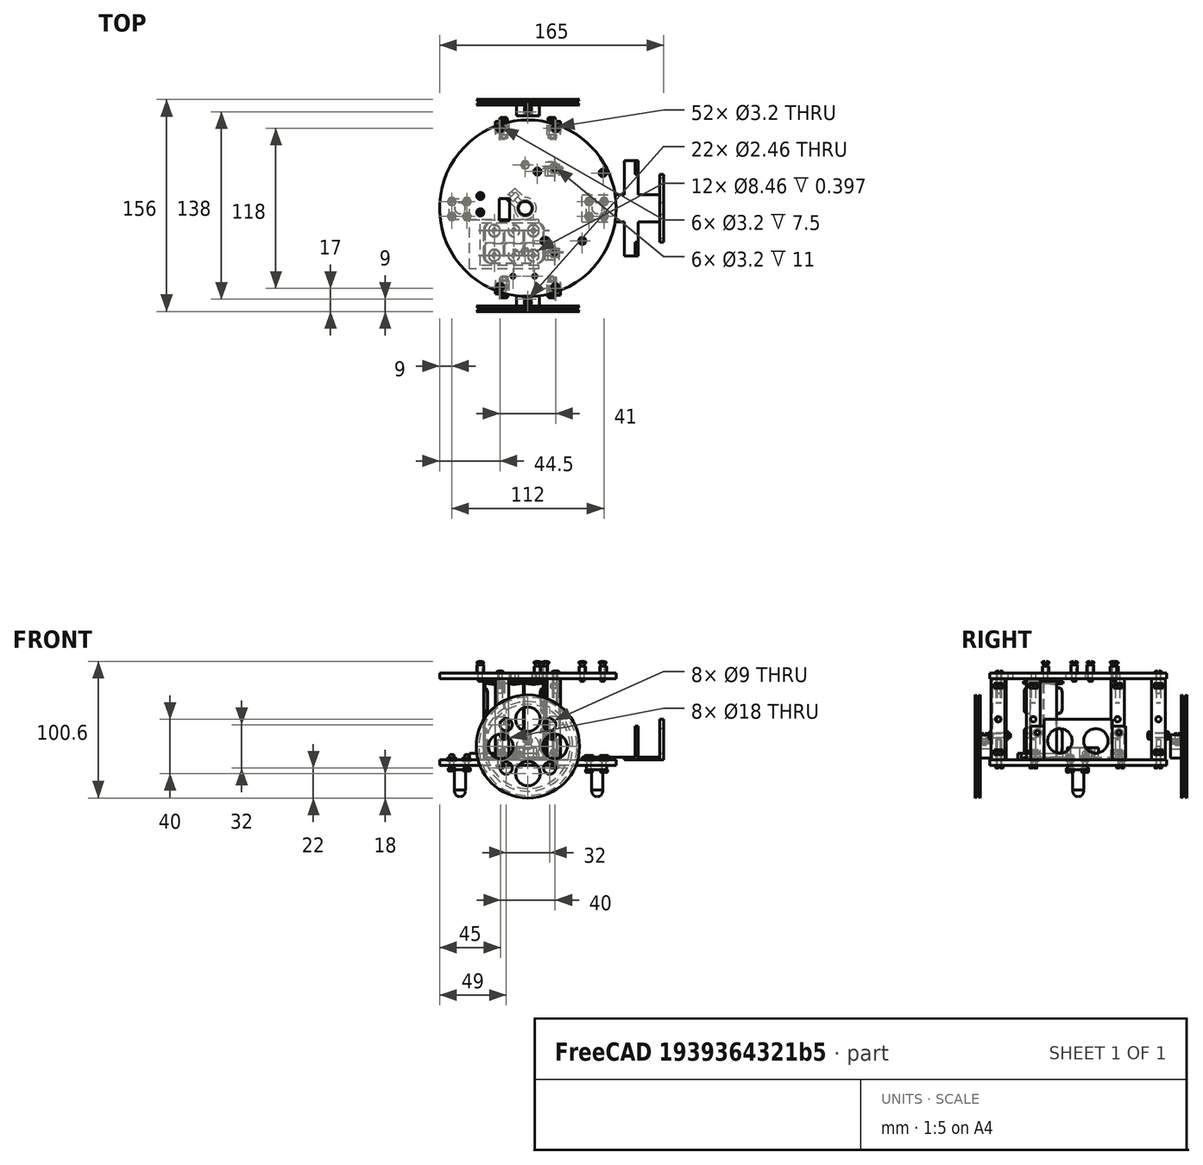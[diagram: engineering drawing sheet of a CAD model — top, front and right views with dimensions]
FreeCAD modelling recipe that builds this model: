
FCSTD DOCUMENT  (FreeCAD 0.21R33668 +26 (Git))
Label: ANIMARUEDASYARDUINO
License: All rights reserved
LicenseURL: https://en.wikipedia.org/wiki/All_rights_reserved
objects: Part::FeaturePython×56, App::DocumentObjectGroupPython×29, Part::MultiFuse×17, Part::Feature×14, Mesh::Feature×5
note: 87 computed .brp shape members not serialized (recipe doc carries the construction recipe); baked Part::Feature solids carry a one-line shape summary decoded from their .brp

FEATURE [Part::Feature] Cut009_solid  label="ballCSensor"
  Placement = pos=(0,0,20) rot=(0,0,1;0rad)
  shape: bbox 15 x 15 x 23 mm, 13 faces (baked)
FEATURE [Part::Feature] Fusion060_solid  label="plataformaInferior (Solid)"
  Placement = pos=(0,0,20) rot=(0,0,1;0rad)
  shape: bbox 130 x 130 x 13 mm, 195 faces (baked)
FEATURE [Part::FeaturePython] Nut  label="M3-Tuerca"  # Fasteners workbench fastener (typed FeaturePython)
  Placement = pos=(41,5,8) rot=(0,0,1;0rad)
  diameter = 4
  invert = false
  leftHanded = false
  matchOuter = false
  offset = 0
  thread = false
  type = 22
FEATURE [Part::FeaturePython] Nut001  label="M3-Tuerca004"  # Fasteners workbench fastener (typed FeaturePython)
  Placement = pos=(52,5,8) rot=(0,0,1;0rad)
  diameter = 4
  invert = false
  leftHanded = false
  matchOuter = false
  offset = 0
  thread = false
  type = 22
FEATURE [Part::FeaturePython] Nut002  label="M3-Tuerca006"  # Fasteners workbench fastener (typed FeaturePython)
  Placement = pos=(52,-6,8) rot=(0,0,1;0rad)
  diameter = 4
  invert = false
  leftHanded = false
  matchOuter = false
  offset = 0
  thread = false
  type = 22
FEATURE [Part::FeaturePython] Nut003  label="M3-Tuerca005"  # Fasteners workbench fastener (typed FeaturePython)
  Placement = pos=(41,-6,8) rot=(0,0,1;0rad)
  diameter = 4
  invert = false
  leftHanded = false
  matchOuter = false
  offset = 0
  thread = false
  type = 22
FEATURE [Part::MultiFuse] Fusion  label="tuercasBallCSensor"
  Placement = pos=(0,0,2) rot=(0,0,1;0rad)
  Shapes = -> [Nut,Nut001,Nut002,Nut003]
FEATURE [Part::FeaturePython] Nut004  label="M3-Tuerca007"  # Fasteners workbench fastener (typed FeaturePython)
  Placement = pos=(41,5,8) rot=(0,0,1;0rad)
  diameter = 4
  invert = false
  leftHanded = false
  matchOuter = false
  offset = 0
  thread = false
  type = 22
FEATURE [Part::FeaturePython] Nut005  label="M3-Tuerca008"  # Fasteners workbench fastener (typed FeaturePython)
  Placement = pos=(52,5,8) rot=(0,0,1;0rad)
  diameter = 4
  invert = false
  leftHanded = false
  matchOuter = false
  offset = 0
  thread = false
  type = 22
FEATURE [Part::FeaturePython] Nut006  label="M3-Tuerca009"  # Fasteners workbench fastener (typed FeaturePython)
  Placement = pos=(52,-6,8) rot=(0,0,1;0rad)
  diameter = 4
  invert = false
  leftHanded = false
  matchOuter = false
  offset = 0
  thread = false
  type = 22
FEATURE [Part::FeaturePython] Nut007  label="M3-Tuerca010"  # Fasteners workbench fastener (typed FeaturePython)
  Placement = pos=(41,-6,8) rot=(0,0,1;0rad)
  diameter = 4
  invert = false
  leftHanded = false
  matchOuter = false
  offset = 0
  thread = false
  type = 22
FEATURE [Part::MultiFuse] Fusion001  label="tuercasBallCLibre"
  Placement = pos=(-101,0,0) rot=(0,0,1;0rad)
  Shapes = -> [Nut004,Nut005,Nut006,Nut007]
FEATURE [Part::Feature] Cut009_solid001  label="ballCLibre"
  Placement = pos=(-101,0,20) rot=(0,0,1;0rad)
  shape: bbox 15 x 15 x 23 mm, 13 faces (baked)
FEATURE [Part::Feature] Cut_solid  label="soporteSensores (Solid)"
  Placement = pos=(15,0,20) rot=(0,0,1;0rad)
  shape: bbox 60 x 70 x 30 mm, 144 faces (baked)
FEATURE [Part::FeaturePython] Screw  label="M3x10-Tornillo"  # Fasteners workbench fastener (typed FeaturePython)
  Placement = pos=(-60,5,3) rot=(1,0,0;3.14159rad)
  diameter = 4
  invert = false
  leftHanded = false
  length = 4
  lengthCustom = 10
  matchOuter = false
  offset = 0
  thread = false
  type = 30
FEATURE [Part::FeaturePython] Screw001  label="M3x10-Tornillo001"  # Fasteners workbench fastener (typed FeaturePython)
  Placement = pos=(-60,-6,3) rot=(1,0,0;3.14159rad)
  diameter = 4
  invert = false
  leftHanded = false
  length = 4
  lengthCustom = 10
  matchOuter = false
  offset = 0
  thread = false
  type = 30
FEATURE [Part::FeaturePython] Screw002  label="M3x10-Tornillo002"  # Fasteners workbench fastener (typed FeaturePython)
  Placement = pos=(-49,-6,3) rot=(1,0,0;3.14159rad)
  diameter = 4
  invert = false
  leftHanded = false
  length = 4
  lengthCustom = 10
  matchOuter = false
  offset = 0
  thread = false
  type = 30
FEATURE [Part::FeaturePython] Screw003  label="M3x10-Tornillo003"  # Fasteners workbench fastener (typed FeaturePython)
  Placement = pos=(-49,5,3) rot=(1,0,0;3.14159rad)
  diameter = 4
  invert = false
  leftHanded = false
  length = 4
  lengthCustom = 10
  matchOuter = false
  offset = 0
  thread = false
  type = 30
FEATURE [Part::MultiFuse] Fusion002  label="tornillosBallClibre"
  Shapes = -> [Screw,Screw001,Screw002,Screw003]
FEATURE [Part::FeaturePython] Screw004  label="M3x10-Tornillo004"  # Fasteners workbench fastener (typed FeaturePython)
  Placement = pos=(-60,5,3) rot=(1,0,0;3.14159rad)
  diameter = 4
  invert = false
  leftHanded = false
  length = 4
  lengthCustom = 10
  matchOuter = false
  offset = 0
  thread = false
  type = 30
FEATURE [Part::FeaturePython] Screw005  label="M3x10-Tornillo005"  # Fasteners workbench fastener (typed FeaturePython)
  Placement = pos=(-60,-6,3) rot=(1,0,0;3.14159rad)
  diameter = 4
  invert = false
  leftHanded = false
  length = 4
  lengthCustom = 10
  matchOuter = false
  offset = 0
  thread = false
  type = 30
FEATURE [Part::FeaturePython] Screw006  label="M3x10-Tornillo006"  # Fasteners workbench fastener (typed FeaturePython)
  Placement = pos=(-49,-6,3) rot=(1,0,0;3.14159rad)
  diameter = 4
  invert = false
  leftHanded = false
  length = 4
  lengthCustom = 10
  matchOuter = false
  offset = 0
  thread = false
  type = 30
FEATURE [Part::FeaturePython] Screw007  label="M3x10-Tornillo007"  # Fasteners workbench fastener (typed FeaturePython)
  Placement = pos=(-49,5,3) rot=(1,0,0;3.14159rad)
  diameter = 4
  invert = false
  leftHanded = false
  length = 4
  lengthCustom = 10
  matchOuter = false
  offset = 0
  thread = false
  type = 30
FEATURE [Part::MultiFuse] Fusion003  label="tornillosBallCSensor"
  Placement = pos=(101,0,-1) rot=(0,0,1;0rad)
  Shapes = -> [Screw004,Screw005,Screw006,Screw007]
FEATURE [App::DocumentObjectGroupPython] SimpleGroup  # scripted group (container) (typed FeaturePython)
  AnimationStepTime = 0
  AnimationSteps = 20
  Distance = 19
  Revolutions = 0
  dir_vectors = (1) [(0,0,1)]
  rot_centers = (1) [(-54.5,-0.5,-14)]
  rot_vectors = (1) [(0,0,1)]
FEATURE [App::DocumentObjectGroupPython] SimpleGroup003  # scripted group (container) (typed FeaturePython)
  AnimationStepTime = 0
  AnimationSteps = 20
  Distance = 20
  Revolutions = 0
  dir_vectors = (1) [(0,0,-1)]
  rot_centers = (1) [(-60,-6,26)]
  rot_vectors = (1) [(0,0,-1)]
FEATURE [App::DocumentObjectGroupPython] SimpleGroup004  # scripted group (container) (typed FeaturePython)
  AnimationStepTime = 0
  AnimationSteps = 20
  Distance = 40
  Revolutions = 0
  dir_vectors = (1) [(0,1.22465e-16,1)]
  rot_centers = (1) [(-60,5,-27)]
  rot_vectors = (1) [(0,1.22465e-16,1)]
FEATURE [App::DocumentObjectGroupPython] SimpleGroup005  # scripted group (container) (typed FeaturePython)
  AnimationStepTime = 0
  AnimationSteps = 20
  Distance = 19
  Revolutions = 0
  dir_vectors = (1) [(0,0,1)]
  rot_centers = (1) [(46.5,-0.5,-14)]
  rot_vectors = (1) [(0,0,1)]
FEATURE [Part::Feature] Part__Feature  label="6 x AAA Holder"
  Placement = pos=(-100,212,67) rot=(0.57735,0.57735,-0.57735;2.0944rad)
  shape: bbox 45.01 x 29.59 x 58.41 mm, 300 faces, 8 solids (baked)
FEATURE [App::DocumentObjectGroupPython] SimpleGroup006  # scripted group (container) (typed FeaturePython)
  AnimationStepTime = 0
  AnimationSteps = 20
  Distance = 100
  Revolutions = 0
  dir_vectors = (1) [(-1,-6.69631e-16,-2.22045e-16)]
  rot_centers = (1) [(13.5,-25.9132,38.8088)]
  rot_vectors = (1) [(-1,-6.69631e-16,-2.22045e-16)]
FEATURE [App::DocumentObjectGroupPython] SimpleGroup007  # scripted group (container) (typed FeaturePython)
  AnimationStepTime = 0
  AnimationSteps = 20
  Distance = 15
  Revolutions = 0
  dir_vectors = (1) [(0,0,-1)]
  rot_centers = (1) [(72,-3.55271e-16,24)]
  rot_vectors = (1) [(0,0,-1)]
FEATURE [App::DocumentObjectGroupPython] SimpleGroup008  # scripted group (container) (typed FeaturePython)
  AnimationStepTime = 0
  AnimationSteps = 20
  Distance = 18
  Revolutions = 0
  dir_vectors = (1) [(0,0,-1)]
  rot_centers = (1) [(52,-6,28)]
  rot_vectors = (1) [(0,0,-1)]
FEATURE [App::DocumentObjectGroupPython] SimpleGroup009  # scripted group (container) (typed FeaturePython)
  AnimationStepTime = 0
  AnimationSteps = 20
  Distance = 39
  Revolutions = 0
  dir_vectors = (1) [(0,0,1)]
  rot_centers = (1) [(52,-6,-27)]
  rot_vectors = (1) [(0,0,1)]
FEATURE [Part::Feature] Cut_solid006  label="columna (Solid)004"
  Placement = pos=(0,-21,0) rot=(0,0,1;0rad)
  shape: bbox 10 x 10 x 60 mm, 24 faces (baked)
FEATURE [Part::Feature] Cut_solid004  label="columna (Solid)002"
  Placement = pos=(-8,21,0) rot=(0,0,1;3.14159rad)
  shape: bbox 10 x 10 x 60 mm, 24 faces (baked)
FEATURE [Part::Feature] Cut_solid007  label="columna (Solid)005"
  Placement = pos=(-8,-96,0) rot=(0,0,1;3.14159rad)
  shape: bbox 10 x 10 x 60 mm, 24 faces (baked)
FEATURE [Part::Feature] Cut_solid003  label="columna (Solid)001"
  Placement = pos=(-1,67,0) rot=(0,0,1;0rad)
  shape: bbox 10 x 10 x 60 mm, 24 faces (baked)
FEATURE [Part::Feature] Cut_solid005  label="columna (Solid)003"
  Placement = pos=(0,97,0) rot=(0,0,1;0rad)
  shape: bbox 10 x 10 x 60 mm, 24 faces (baked)
FEATURE [Part::FeaturePython] Screw008  label="M3x10-Tornillo008"  # Fasteners workbench fastener (typed FeaturePython)
  Placement = pos=(-24.5,-58,5) rot=(1,0,0;3.14159rad)
  diameter = 4
  invert = false
  leftHanded = false
  length = 4
  lengthCustom = 10
  matchOuter = false
  offset = 0
  thread = false
  type = 30
FEATURE [Part::FeaturePython] Screw009  label="M3x10-Tornillo009"  # Fasteners workbench fastener (typed FeaturePython)
  Placement = pos=(16.5,-58,5) rot=(1,0,0;3.14159rad)
  diameter = 4
  invert = false
  leftHanded = false
  length = 4
  lengthCustom = 10
  matchOuter = false
  offset = 0
  thread = false
  type = 30
FEATURE [Part::FeaturePython] Screw010  label="M3x10-Tornillo010"  # Fasteners workbench fastener (typed FeaturePython)
  Placement = pos=(15.5,-33,5) rot=(1,0,0;3.14159rad)
  diameter = 4
  invert = false
  leftHanded = false
  length = 4
  lengthCustom = 10
  matchOuter = false
  offset = 0
  thread = false
  type = 30
FEATURE [Part::FeaturePython] Screw011  label="M3x10-Tornillo011"  # Fasteners workbench fastener (typed FeaturePython)
  Placement = pos=(15.5,31,5) rot=(1,0,0;3.14159rad)
  diameter = 4
  invert = false
  leftHanded = false
  length = 4
  lengthCustom = 10
  matchOuter = false
  offset = 0
  thread = false
  type = 30
FEATURE [Part::FeaturePython] Screw012  label="M3x10-Tornillo012"  # Fasteners workbench fastener (typed FeaturePython)
  Placement = pos=(16.5,59,5) rot=(1,0,0;3.14159rad)
  diameter = 4
  invert = false
  leftHanded = false
  length = 4
  lengthCustom = 10
  matchOuter = false
  offset = 0
  thread = false
  type = 30
FEATURE [Part::FeaturePython] Screw013  label="M3x14-Tornillo"  # Fasteners workbench fastener (typed FeaturePython)
  Placement = pos=(-24.5,59,5) rot=(1,0,0;3.14159rad)
  diameter = 4
  invert = false
  leftHanded = false
  length = 6
  lengthCustom = 14
  matchOuter = false
  offset = 0
  thread = false
  type = 30
FEATURE [Part::Feature] Cut_solid002  label="columna (Solid)"
  Placement = pos=(-1,5,0) rot=(0,0,1;0rad)
  shape: bbox 10 x 10 x 60 mm, 24 faces (baked)
FEATURE [Part::MultiFuse] Fusion004  label="columnas"
  Placement = pos=(0,0,20) rot=(0,0,1;0rad)
  Shapes = -> [Cut_solid006,Cut_solid004,Cut_solid007,Cut_solid003,Cut_solid005,Cut_solid002]
FEATURE [Part::MultiFuse] Fusion005  label="tornillosAbajo"
  Shapes = -> [Screw008,Screw009,Screw010,Screw011,Screw012,Screw013]
FEATURE [Part::FeaturePython] Nut008  label="M3-Tuerca011"  # Fasteners workbench fastener (typed FeaturePython)
  Placement = pos=(16,30,23) rot=(0,0,1;0rad)
  diameter = 4
  invert = false
  leftHanded = false
  matchOuter = false
  offset = 0
  thread = false
  type = 22
FEATURE [Part::FeaturePython] Nut009  label="M3-Tuerca012"  # Fasteners workbench fastener (typed FeaturePython)
  Placement = pos=(16,-32,23) rot=(0,0,1;0rad)
  diameter = 4
  invert = false
  leftHanded = false
  matchOuter = false
  offset = 0
  thread = false
  type = 22
FEATURE [Part::FeaturePython] Nut010  label="M3-Tuerca013"  # Fasteners workbench fastener (typed FeaturePython)
  Placement = pos=(16,-59,23) rot=(0,0,1;0rad)
  diameter = 4
  invert = false
  leftHanded = false
  matchOuter = false
  offset = 0
  thread = false
  type = 22
FEATURE [Part::FeaturePython] Nut011  label="M3-Tuerca014"  # Fasteners workbench fastener (typed FeaturePython)
  Placement = pos=(16,-59,72) rot=(0,0,1;0rad)
  diameter = 4
  invert = false
  leftHanded = false
  matchOuter = false
  offset = 0
  thread = false
  type = 22
FEATURE [Part::FeaturePython] Nut012  label="M3-Tuerca015"  # Fasteners workbench fastener (typed FeaturePython)
  Placement = pos=(16,-33,72) rot=(0,0,1;0rad)
  diameter = 4
  invert = false
  leftHanded = false
  matchOuter = false
  offset = 0
  thread = false
  type = 22
FEATURE [Part::FeaturePython] Nut013  label="M3-Tuerca016"  # Fasteners workbench fastener (typed FeaturePython)
  Placement = pos=(16,29,72) rot=(0,0,1;0rad)
  diameter = 4
  invert = false
  leftHanded = false
  matchOuter = false
  offset = 0
  thread = false
  type = 22
FEATURE [Part::FeaturePython] Nut014  label="M3-Tuerca017"  # Fasteners workbench fastener (typed FeaturePython)
  Placement = pos=(16,59,72) rot=(0,0,1;0rad)
  diameter = 4
  invert = false
  leftHanded = false
  matchOuter = false
  offset = 0
  thread = false
  type = 22
FEATURE [Part::FeaturePython] Nut015  label="M3-Tuerca018"  # Fasteners workbench fastener (typed FeaturePython)
  Placement = pos=(16,59,23) rot=(0,0,1;0.523599rad)
  diameter = 4
  invert = false
  leftHanded = false
  matchOuter = false
  offset = 0
  thread = false
  type = 22
FEATURE [Part::MultiFuse] Fusion006  label="tuercasDelante"
  Placement = pos=(0,0,-10) rot=(0,0,1;0rad)
  Shapes = -> [Nut015,Nut008,Nut009,Nut010,Nut011,Nut012,Nut013,Nut014]
FEATURE [App::DocumentObjectGroupPython] SimpleGroup010  # scripted group (container) (typed FeaturePython)
  AnimationStepTime = 0
  AnimationSteps = 20
  Distance = 20
  Revolutions = 0
  dir_vectors = (1) [(-1,5.55112e-16,0)]
  rot_centers = (1) [(38.25,59,24.2)]
  rot_vectors = (1) [(-1,5.55112e-16,0)]
FEATURE [Part::FeaturePython] Nut016  label="M3-Tuerca021"  # Fasteners workbench fastener (typed FeaturePython)
  Placement = pos=(-25,59,23) rot=(0,0,1;0.523599rad)
  diameter = 4
  invert = false
  leftHanded = false
  matchOuter = false
  offset = 0
  thread = false
  type = 22
FEATURE [Part::FeaturePython] Nut017  label="M3-Tuerca022"  # Fasteners workbench fastener (typed FeaturePython)
  Placement = pos=(-25,59,72) rot=(0,0,1;0.523599rad)
  diameter = 4
  invert = false
  leftHanded = false
  matchOuter = false
  offset = 0
  thread = false
  type = 22
FEATURE [Part::FeaturePython] Nut018  label="M3-Tuerca023"  # Fasteners workbench fastener (typed FeaturePython)
  Placement = pos=(-25,-58,72) rot=(0,0,1;0.523599rad)
  diameter = 4
  invert = false
  leftHanded = false
  matchOuter = false
  offset = 0
  thread = false
  type = 22
FEATURE [Part::FeaturePython] Nut019  label="M3-Tuerca024"  # Fasteners workbench fastener (typed FeaturePython)
  Placement = pos=(-25,-58,23) rot=(0,0,1;0.523599rad)
  diameter = 4
  invert = false
  leftHanded = false
  matchOuter = false
  offset = 0
  thread = false
  type = 22
FEATURE [Part::MultiFuse] Fusion007  label="tuercasAtras"
  Placement = pos=(0,0,-10) rot=(0,0,1;0rad)
  Shapes = -> [Nut019,Nut016,Nut017,Nut018]
FEATURE [App::DocumentObjectGroupPython] SimpleGroup011  # scripted group (container) (typed FeaturePython)
  AnimationStepTime = 0
  AnimationSteps = 20
  Distance = 20
  Revolutions = 0
  dir_vectors = (1) [(1,-1.66533e-16,0)]
  rot_centers = (1) [(-42.25,-58,73.2)]
  rot_vectors = (1) [(1,-1.66533e-16,0)]
FEATURE [App::DocumentObjectGroupPython] SimpleGroup012  # scripted group (container) (typed FeaturePython)
  AnimationStepTime = 0
  AnimationSteps = 20
  Distance = -10
  Revolutions = 0
  dir_vectors = (3) [(0,0,1),(0,0,1),(0,0,1)]
  rot_centers = (3) [(-2.75414,1.04693,9),(-2.75414,1.04693,9),(-2.75414,1.04693,9)]
  rot_vectors = (3) [(0,0,1),(0,0,1),(0,0,1)]
FEATURE [App::DocumentObjectGroupPython] SimpleGroup013  # scripted group (container) (typed FeaturePython)
  AnimationStepTime = 0
  AnimationSteps = 20
  Distance = -20
  Revolutions = 0
  dir_vectors = (1) [(0,0,-1)]
  rot_centers = (1) [(-4.00424,0.00296236,5)]
  rot_vectors = (1) [(0,0,-1)]
FEATURE [Mesh::Feature] _8BYJ_48_v007  label="28BYJ-48_v007"
  Placement = pos=(-8.5,-31,24.5) rot=(0,0,1;3.14159rad)
FEATURE [Mesh::Feature] _8BYJ_48_v6  label="28BYJ-48_v6"
  Placement = pos=(0.5,32,25) rot=(0,0,1;0rad)
FEATURE [Part::FeaturePython] Screw014  label="M3x14-Tornillo006"  # Fasteners workbench fastener (typed FeaturePython)
  Placement = pos=(-21.5,-64,27) rot=(1,0,0;1.5708rad)
  diameter = 4
  invert = false
  leftHanded = false
  length = 5
  lengthCustom = 14
  matchOuter = false
  offset = 0
  thread = false
  type = 36
FEATURE [Part::FeaturePython] Screw015  label="M3x14-Tornillo007"  # Fasteners workbench fastener (typed FeaturePython)
  Placement = pos=(13.5,-64,27) rot=(1,0,0;1.5708rad)
  diameter = 4
  invert = false
  leftHanded = false
  length = 5
  lengthCustom = 14
  matchOuter = false
  offset = 0
  thread = false
  type = 36
FEATURE [Part::FeaturePython] Screw016  label="M3x14-Tornillo005"  # Fasteners workbench fastener (typed FeaturePython)
  Placement = pos=(13.5,65,27) rot=(0,0.707107,0.707107;3.14159rad)
  diameter = 4
  invert = false
  leftHanded = false
  length = 5
  lengthCustom = 14
  matchOuter = false
  offset = 0
  thread = false
  type = 36
FEATURE [Part::FeaturePython] Screw017  label="M3x14-Tornillo004"  # Fasteners workbench fastener (typed FeaturePython)
  Placement = pos=(-22,65,27) rot=(0,0.707107,0.707107;3.14159rad)
  diameter = 4
  invert = false
  leftHanded = false
  length = 5
  lengthCustom = 14
  matchOuter = false
  offset = 0
  thread = false
  type = 36
FEATURE [Part::FeaturePython] Nut020  label="M3-Tuerca025"  # Fasteners workbench fastener (typed FeaturePython)
  Placement = pos=(-22,54,27) rot=(1,0,0;1.5708rad)
  diameter = 4
  invert = false
  leftHanded = false
  matchOuter = false
  offset = 0
  thread = false
  type = 22
FEATURE [Part::FeaturePython] Nut021  label="M3-Tuerca026"  # Fasteners workbench fastener (typed FeaturePython)
  Placement = pos=(14,54,27) rot=(1,0,0;1.5708rad)
  diameter = 4
  invert = false
  leftHanded = false
  matchOuter = false
  offset = 0
  thread = false
  type = 22
FEATURE [Part::FeaturePython] Nut022  label="M3-Tuerca027"  # Fasteners workbench fastener (typed FeaturePython)
  Placement = pos=(14,-51,27) rot=(1,0,0;1.5708rad)
  diameter = 4
  invert = false
  leftHanded = false
  matchOuter = false
  offset = 0
  thread = false
  type = 22
FEATURE [Part::FeaturePython] Nut023  label="M3-Tuerca028"  # Fasteners workbench fastener (typed FeaturePython)
  Placement = pos=(-21.5,-51,27) rot=(1,0,0;1.5708rad)
  diameter = 4
  invert = false
  leftHanded = false
  matchOuter = false
  offset = 0
  thread = false
  type = 22
FEATURE [Part::MultiFuse] Fusion008  label="tornillosDerecha"
  Shapes = -> [Screw014,Screw015]
FEATURE [Part::MultiFuse] Fusion009  label="tuercasDerecha"
  Shapes = -> [Nut022,Nut023]
FEATURE [App::DocumentObjectGroupPython] SimpleGroup014  # scripted group (container) (typed FeaturePython)
  AnimationStepTime = 0
  AnimationSteps = 20
  Distance = -20
  Revolutions = 0
  dir_vectors = (1) [(0,-1,0)]
  rot_centers = (1) [(-23.023,-63,39.1844)]
  rot_vectors = (1) [(0,-1,0)]
FEATURE [App::DocumentObjectGroupPython] SimpleGroup015  # scripted group (container) (typed FeaturePython)
  AnimationStepTime = 0
  AnimationSteps = 20
  Distance = -40
  Revolutions = 0
  dir_vectors = (1) [(0,-1,0)]
  rot_centers = (1) [(-23.023,-63,39.1844)]
  rot_vectors = (1) [(0,-1,0)]
FEATURE [App::DocumentObjectGroupPython] SimpleGroup016  # scripted group (container) (typed FeaturePython)
  AnimationStepTime = 0
  AnimationSteps = 20
  Distance = -10
  Revolutions = 0
  dir_vectors = (1) [(0,1,0)]
  rot_centers = (1) [(-23.023,-53,39.1844)]
  rot_vectors = (1) [(0,1,0)]
FEATURE [Part::MultiFuse] Fusion010  label="tornillosIzquierda"
  Shapes = -> [Screw016,Screw017]
FEATURE [Part::MultiFuse] Fusion011  label="tuercasIzquierda"
  Shapes = -> [Nut020,Nut021]
FEATURE [App::DocumentObjectGroupPython] SimpleGroup017  # scripted group (container) (typed FeaturePython)
  AnimationStepTime = 0
  AnimationSteps = 20
  Distance = -20
  Revolutions = 0
  dir_vectors = (1) [(0,1,0)]
  rot_centers = (1) [(-23.023,64,49.1844)]
  rot_vectors = (1) [(0,1,0)]
FEATURE [App::DocumentObjectGroupPython] SimpleGroup018  # scripted group (container) (typed FeaturePython)
  AnimationStepTime = 0
  AnimationSteps = 20
  Distance = -40
  Revolutions = 0
  dir_vectors = (1) [(0,1,0)]
  rot_centers = (1) [(-23.023,64,39.1844)]
  rot_vectors = (1) [(0,1,0)]
FEATURE [App::DocumentObjectGroupPython] SimpleGroup019  # scripted group (container) (typed FeaturePython)
  AnimationStepTime = 0
  AnimationSteps = 20
  Distance = 10
  Revolutions = 0
  dir_vectors = (1) [(0,1,0)]
  rot_centers = (1) [(-23.023,64,39.1844)]
  rot_vectors = (1) [(0,1,0)]
FEATURE [Part::Feature] Cut_solid008  label="plataformaSuperior (Solid)"
  Placement = pos=(0,0,20) rot=(0,0,1;0rad)
  shape: bbox 130 x 130 x 10 mm, 42 faces (baked)
FEATURE [Part::FeaturePython] Screw018  label="M3x16-Tornillo"  # Fasteners workbench fastener (typed FeaturePython)
  Placement = pos=(16.5,59,74) rot=(0,0,1;0rad)
  diameter = 4
  invert = false
  leftHanded = false
  length = 6
  lengthCustom = 16
  matchOuter = false
  offset = 0
  thread = false
  type = 38
FEATURE [Part::FeaturePython] Screw019  label="M3x16-Tornillo001"  # Fasteners workbench fastener (typed FeaturePython)
  Placement = pos=(-24.5,59,74) rot=(0,0,1;0rad)
  diameter = 4
  invert = false
  leftHanded = false
  length = 6
  lengthCustom = 16
  matchOuter = false
  offset = 0
  thread = false
  type = 38
FEATURE [Part::FeaturePython] Screw020  label="M3x16-Tornillo002"  # Fasteners workbench fastener (typed FeaturePython)
  Placement = pos=(-24.5,-58,74) rot=(0,0,1;0rad)
  diameter = 4
  invert = false
  leftHanded = false
  length = 6
  lengthCustom = 16
  matchOuter = false
  offset = 0
  thread = false
  type = 38
FEATURE [Part::FeaturePython] Screw021  label="M3x16-Tornillo003"  # Fasteners workbench fastener (typed FeaturePython)
  Placement = pos=(16.2,-58,74) rot=(0,0,1;0rad)
  diameter = 4
  invert = false
  leftHanded = false
  length = 6
  lengthCustom = 16
  matchOuter = false
  offset = 0
  thread = false
  type = 38
FEATURE [Part::MultiFuse] Fusion012  label="tornillosSuperiorIzquierda"
  Shapes = -> [Screw018,Screw019]
FEATURE [Part::MultiFuse] Fusion013  label="tornillosSuperiorDerecha"
  Shapes = -> [Screw020,Screw021]
FEATURE [App::DocumentObjectGroupPython] SimpleGroup020  # scripted group (container) (typed FeaturePython)
  AnimationStepTime = 0
  AnimationSteps = 20
  Distance = -20
  Revolutions = 0
  dir_vectors = (1) [(0,0,1)]
  rot_centers = (1) [(-22.8688,-58,69)]
  rot_vectors = (1) [(0,0,1)]
FEATURE [App::DocumentObjectGroupPython] SimpleGroup021  # scripted group (container) (typed FeaturePython)
  AnimationStepTime = 0
  AnimationSteps = 20
  Distance = -40
  Revolutions = 0
  dir_vectors = (2) [(0,0,1),(0,0,1)]
  rot_centers = (2) [(-3.91562,0.0566826,73),(-3.91562,0.0566826,73)]
  rot_vectors = (2) [(0,0,1),(0,0,1)]
FEATURE [Part::Feature] Part_solid  label="ruedaIzquierda"
  Placement = pos=(-4,79,19) rot=(-1,0,0;1.5708rad)
  shape: bbox 76 x 12 x 76 mm, 29 faces (baked)
FEATURE [Part::Feature] Part_solid001  label="ruedaDerecha"
  Placement = pos=(-4,-75,19) rot=(0,0.707107,-0.707107;3.14159rad)
  shape: bbox 76 x 12 x 76 mm, 29 faces (baked)
FEATURE [Part::FeaturePython] Nut024  label="M3-Tuerca085"  # Fasteners workbench fastener (typed FeaturePython)
  Placement = pos=(-4,71,22) rot=(0,0,1;0rad)
  diameter = 4
  invert = false
  leftHanded = false
  matchOuter = false
  offset = 0
  thread = false
  type = 22
FEATURE [Part::FeaturePython] Screw022  label="M3x8-Tornillo"  # Fasteners workbench fastener (typed FeaturePython)
  Placement = pos=(-4,73,28) rot=(0,0,1;0rad)
  diameter = 4
  invert = false
  leftHanded = false
  length = 2
  lengthCustom = 8
  matchOuter = false
  offset = 0
  thread = false
  type = 38
FEATURE [Part::FeaturePython] Nut025  label="M3-Tuerca086"  # Fasteners workbench fastener (typed FeaturePython)
  Placement = pos=(-4,-67,22) rot=(0,0,1;0rad)
  diameter = 4
  invert = false
  leftHanded = false
  matchOuter = false
  offset = 0
  thread = false
  type = 22
FEATURE [App::DocumentObjectGroupPython] SimpleGroup022  # scripted group (container) (typed FeaturePython)
  AnimationStepTime = 0
  AnimationSteps = 20
  Distance = -10
  Revolutions = 0
  dir_vectors = (1) [(0,-1,0)]
  rot_centers = (1) [(-4,88,18.6699)]
  rot_vectors = (1) [(0,-1,0)]
FEATURE [App::DocumentObjectGroupPython] SimpleGroup023  # scripted group (container) (typed FeaturePython)
  AnimationStepTime = 0
  AnimationSteps = 20
  Distance = -10
  Revolutions = 0
  dir_vectors = (1) [(0,0,1)]
  rot_centers = (1) [(-2.75414,1.04693,9)]
  rot_vectors = (1) [(0,0,1)]
FEATURE [App::DocumentObjectGroupPython] SimpleGroup024  # scripted group (container) (typed FeaturePython)
  AnimationStepTime = 0
  AnimationSteps = 20
  Distance = -20
  Revolutions = 0
  dir_vectors = (3) [(0,1,0),(0,1,0),(0,1,0)]
  rot_centers = (3) [(15.023,64,39.1844),(15.023,64,39.1844),(15.023,64,39.1844)]
  rot_vectors = (3) [(0,1,0),(0,1,0),(0,1,0)]
FEATURE [Part::FeaturePython] Screw023  label="M3x8-Tornillo001"  # Fasteners workbench fastener (typed FeaturePython)
  Placement = pos=(-4,-69,28) rot=(0,0,1;0rad)
  diameter = 4
  invert = false
  leftHanded = false
  length = 2
  lengthCustom = 8
  matchOuter = false
  offset = 0
  thread = false
  type = 38
FEATURE [App::DocumentObjectGroupPython] SimpleGroup025  # scripted group (container) (typed FeaturePython)
  AnimationStepTime = 0
  AnimationSteps = 20
  Distance = -10
  Revolutions = 0
  dir_vectors = (1) [(0,1,2.22045e-16)]
  rot_centers = (1) [(-4,-88,18.6699)]
  rot_vectors = (1) [(0,1,2.22045e-16)]
FEATURE [App::DocumentObjectGroupPython] SimpleGroup026  # scripted group (container) (typed FeaturePython)
  AnimationStepTime = 0
  AnimationSteps = 20
  Distance = -10
  Revolutions = 0
  dir_vectors = (1) [(0,0,1)]
  rot_centers = (1) [(14.8688,-59,69)]
  rot_vectors = (1) [(0,0,1)]
FEATURE [App::DocumentObjectGroupPython] SimpleGroup027  # scripted group (container) (typed FeaturePython)
  AnimationStepTime = 0
  AnimationSteps = 20
  Distance = -24
  Revolutions = 0
  dir_vectors = (3) [(0,-1,0),(0,-1,0),(0,-1,0)]
  rot_centers = (3) [(15.023,-64,39.1844),(15.023,-64,39.1844),(15.023,-64,39.1844)]
  rot_vectors = (3) [(0,-1,0),(0,-1,0),(0,-1,0)]
FEATURE [Mesh::Feature] Arduino_ipt001  label="Arduino.ipt001"
  Placement = pos=(-8,15,110) rot=(0,0,1;3.14159rad)
FEATURE [Mesh::Feature] ULN2003_Stepper_Driver001
  Placement = pos=(-51.5,24.5,79) rot=(0,0,1;0rad)
FEATURE [Mesh::Feature] ULN2003_Stepper_Driver
  Placement = pos=(-51.5,-18.5,79) rot=(0,0,1;0rad)
FEATURE [Part::FeaturePython] Screw024  label="M3x14-Tornillo008"  # Fasteners workbench fastener (typed FeaturePython)
  Placement = pos=(3,27,81) rot=(0,0,1;0rad)
  diameter = 4
  invert = false
  leftHanded = false
  length = 10
  lengthCustom = 14
  matchOuter = false
  offset = 0
  thread = false
  type = 38
FEATURE [Part::FeaturePython] Screw025  label="M3x14-Tornillo009"  # Fasteners workbench fastener (typed FeaturePython)
  Placement = pos=(51,26,81) rot=(0,0,1;0rad)
  diameter = 4
  invert = false
  leftHanded = false
  length = 10
  lengthCustom = 14
  matchOuter = false
  offset = 0
  thread = false
  type = 38
FEATURE [Part::FeaturePython] Screw026  label="M3x14-Tornillo010"  # Fasteners workbench fastener (typed FeaturePython)
  Placement = pos=(36,-24,81) rot=(0,0,1;0rad)
  diameter = 4
  invert = false
  leftHanded = false
  length = 5
  lengthCustom = 14
  matchOuter = false
  offset = 0
  thread = false
  type = 38
FEATURE [Part::FeaturePython] Screw027  label="M3x14-Tornillo011"  # Fasteners workbench fastener (typed FeaturePython)
  Placement = pos=(9,-24,81) rot=(0,0,1;0rad)
  diameter = 4
  invert = false
  leftHanded = false
  length = 5
  lengthCustom = 14
  matchOuter = false
  offset = 0
  thread = false
  type = 38
FEATURE [Part::MultiFuse] Fusion014  label="tornillosArduino"
  Shapes = -> [Screw027,Screw024,Screw025,Screw026]
FEATURE [Part::FeaturePython] Screw028  label="M3x14-Tornillo012"  # Fasteners workbench fastener (typed FeaturePython)
  Placement = pos=(-39,-3,81) rot=(0,0,1;0rad)
  diameter = 4
  invert = false
  leftHanded = false
  length = 5
  lengthCustom = 14
  matchOuter = false
  offset = 0
  thread = false
  type = 38
FEATURE [Part::FeaturePython] Screw029  label="M3x14-Tornillo013"  # Fasteners workbench fastener (typed FeaturePython)
  Placement = pos=(-39,9,81) rot=(0,0,1;0rad)
  diameter = 4
  invert = false
  leftHanded = false
  length = 5
  lengthCustom = 14
  matchOuter = false
  offset = 0
  thread = false
  type = 38
FEATURE [Part::MultiFuse] Fusion015  label="tornillosULN2003"
  Shapes = -> [Screw029,Screw028]
FEATURE [Part::MultiFuse] Fusion016  label="tornillosCircuitos"
  Shapes = -> [Fusion015,Fusion014]
FEATURE [App::DocumentObjectGroupPython] SimpleGroup028  # scripted group (container) (typed FeaturePython)
  AnimationStepTime = 0
  AnimationSteps = 20
  Distance = -20
  Revolutions = 0
  dir_vectors = (3) [(0,0,1),(0,0,1),(0,0,1)]
  rot_centers = (3) [(-3.91562,0.0566826,73),(-3.91562,0.0566826,73),(-3.91562,0.0566826,73)]
  rot_vectors = (3) [(0,0,1),(0,0,1),(0,0,1)]
FEATURE [App::DocumentObjectGroupPython] SimpleGroup029  # scripted group (container) (typed FeaturePython)
  AnimationStepTime = 0
  AnimationSteps = 20
  Distance = -40
  Revolutions = 0
  dir_vectors = (1) [(0,0,1)]
  rot_centers = (1) [(-3.91562,0.0566826,73)]
  rot_vectors = (1) [(0,0,1)]
FEATURE [App::DocumentObjectGroupPython] ExplodedAssembly  # scripted group (container) (typed FeaturePython)
  AnimationStep = 0
  CurrentTrajectory = -1
  Group = -> [SimpleGroup,SimpleGroup003,SimpleGroup004,SimpleGroup005,SimpleGroup006,SimpleGroup007,SimpleGroup008,SimpleGroup009,SimpleGroup010,SimpleGroup011,SimpleGroup012,SimpleGroup013,SimpleGroup014,SimpleGroup015,SimpleGroup016,SimpleGroup017,SimpleGroup018,SimpleGroup019,SimpleGroup020,SimpleGroup021,SimpleGroup022,SimpleGroup023,SimpleGroup024,SimpleGroup025,SimpleGroup026,SimpleGroup027,+2 more]
  InAnimation = false
  RemoveAllTrajectories = false
  ResetAnimation = false
